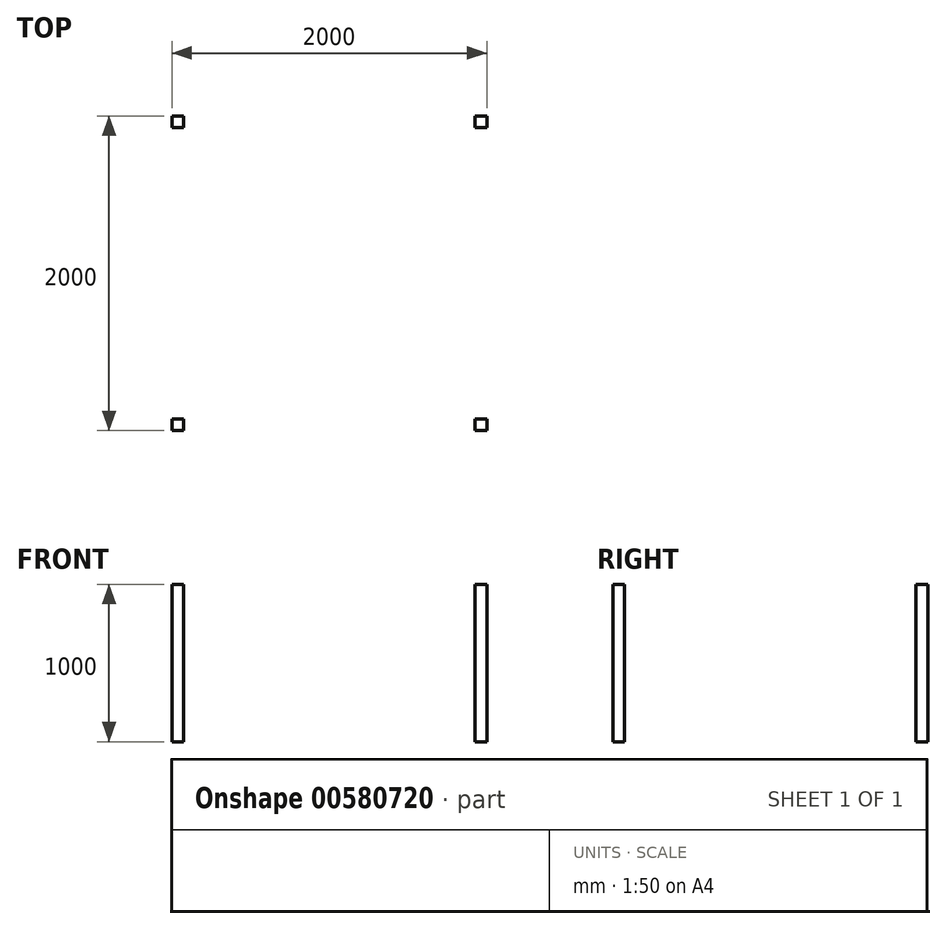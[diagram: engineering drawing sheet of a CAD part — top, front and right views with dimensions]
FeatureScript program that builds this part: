
annotation { "Feature Type Name" : "Feature", "Feature Type Description" : "" }
export const myFeature = defineFeature(function(context is Context, id is Id, definition is map)
    precondition{}
    {
        {
            var Q0;
            Q0=qCreatedBy(makeId("Top.planeOp"),FACE);
            var sketch = newSketch(context, id + "F0", { "sketchPlane" : qUnion([Q0])});
            skLineSegment(sketch, "E0.bottom", {"start": v(-1000, 1000) * mm, "end": v(-926, 1000) * mm});
            skLineSegment(sketch, "E0.top", {"start": v(-1000, 926) * mm, "end": v(-926, 926) * mm});
            skLineSegment(sketch, "E0.left", {"start": v(-1000, 1000) * mm, "end": v(-1000, 926) * mm});
            skLineSegment(sketch, "E0.right", {"start": v(-926, 1000) * mm, "end": v(-926, 926) * mm});
            skLineSegment(sketch, "E1.MirrorCS", {"start": v(1000, 1000) * mm, "end": v(926, 1000) * mm});
            skLineSegment(sketch, "E2.MirrorCS", {"start": v(1000, 1000) * mm, "end": v(1000, 926) * mm});
            skLineSegment(sketch, "E3.MirrorCS", {"start": v(926, 1000) * mm, "end": v(926, 926) * mm});
            skLineSegment(sketch, "E4.MirrorCS", {"start": v(1000, 926) * mm, "end": v(926, 926) * mm});
            skLineSegment(sketch, "E5.MirrorCS", {"start": v(1000, -926) * mm, "end": v(926, -926) * mm});
            skLineSegment(sketch, "E6.MirrorCS", {"start": v(926, -1000) * mm, "end": v(926, -926) * mm});
            skLineSegment(sketch, "E7.MirrorCS", {"start": v(-1000, -1000) * mm, "end": v(-926, -1000) * mm});
            skLineSegment(sketch, "E8.MirrorCS", {"start": v(-1000, -926) * mm, "end": v(-926, -926) * mm});
            skLineSegment(sketch, "E9.MirrorCS", {"start": v(-1000, -1000) * mm, "end": v(-1000, -926) * mm});
            skLineSegment(sketch, "E10.MirrorCS", {"start": v(-926, -1000) * mm, "end": v(-926, -926) * mm});
            skLineSegment(sketch, "E11.MirrorCS", {"start": v(1000, -1000) * mm, "end": v(926, -1000) * mm});
            skLineSegment(sketch, "E12.MirrorCS", {"start": v(1000, -1000) * mm, "end": v(1000, -926) * mm});
            skSolve(sketch);
        }
        {
            var Q0;
            Q0 = qSketchRegion(id + "F0", true);
            extrude(context, id + "F1", {"entities" : qUnion([Q0]), "depth" : 1000 * mm, "offsetDistance" : 25 * mm});
        }
    });
